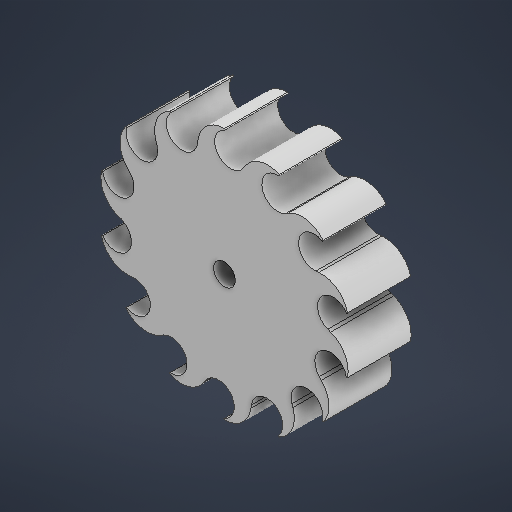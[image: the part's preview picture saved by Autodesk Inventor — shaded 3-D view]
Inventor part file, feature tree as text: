
AUTODESK INVENTOR PART (.ipt)
format: ipt  version: 2025.3 (Build 293356030, 356C)  size: 331,264 bytes
history: native  units: mm
features: sketch x2, extrude x1
ambient origin geometry x8: Origin, YZ Plane, XZ Plane, XY Plane, X Axis, Y Axis, Z Axis, Center Point
bodies: Solid1 (feature_tree)
feature tree (3):
  extrude  "Extrusion1"  Depth=60.0mm
  sketch  "Sketch1"  dims[d6=80.0mm d14=60.0mm]
  sketch  "Sketch Circular Pattern5"  dims[d16=0.2mm d22=5.0mm d23=60.0deg d28=6.0mm d29=140.0mm d31=360.0deg d33=6.9mm d34=20.0mm d35=0.0mm]
